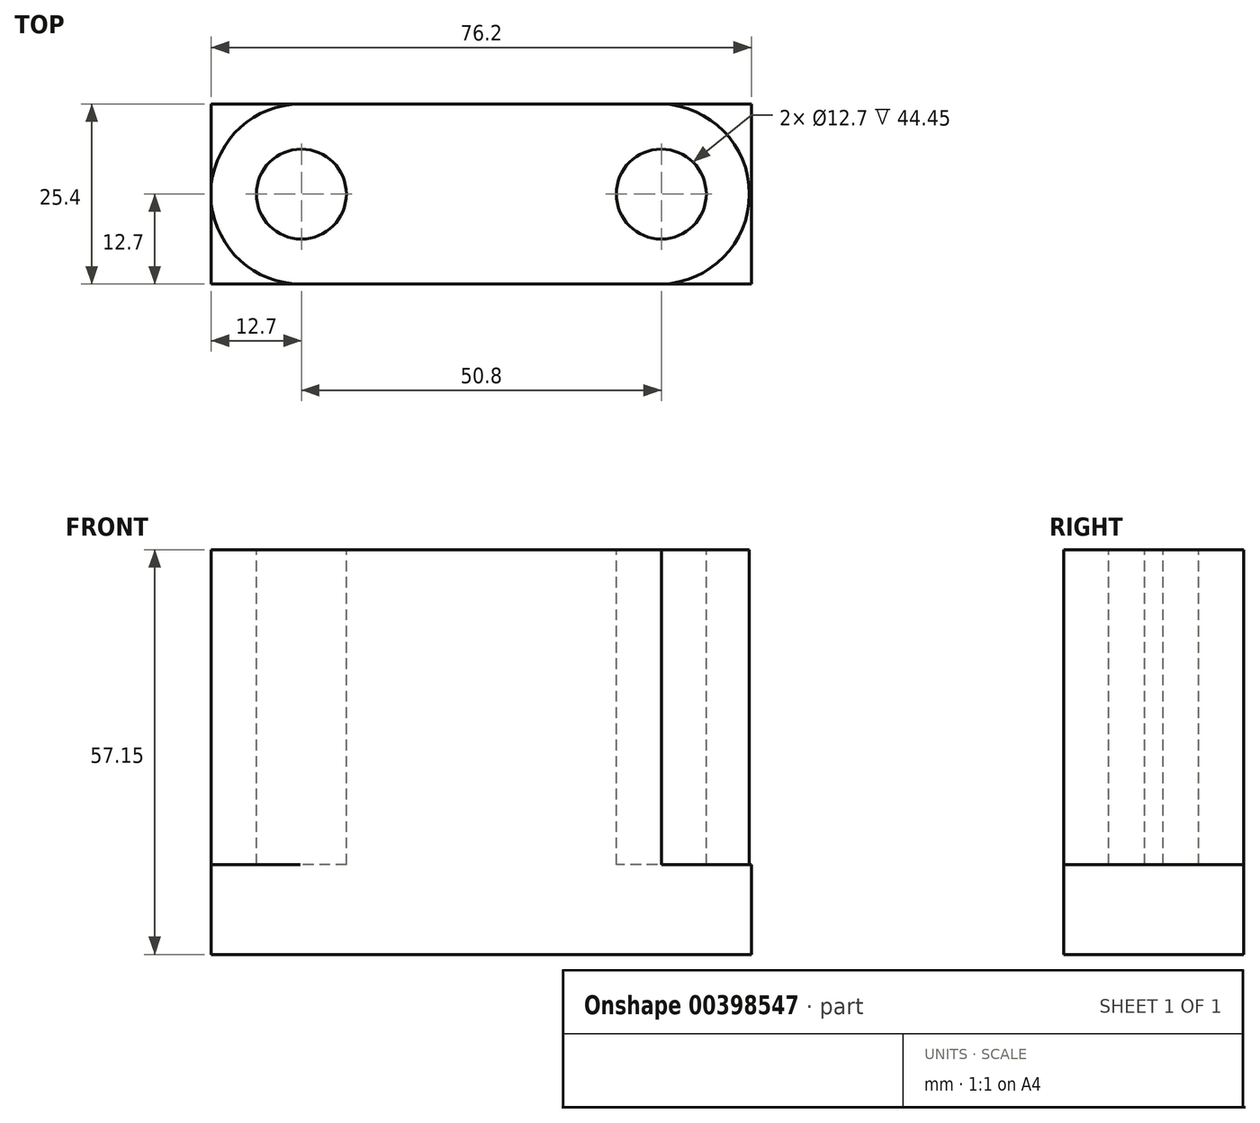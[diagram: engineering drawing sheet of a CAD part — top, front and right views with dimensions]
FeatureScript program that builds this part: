
annotation { "Feature Type Name" : "Feature", "Feature Type Description" : "" }
export const myFeature = defineFeature(function(context is Context, id is Id, definition is map)
    precondition{}
    {
        {
            var Q0;
            Q0=qCreatedBy(makeId("Front.planeOp"),FACE);
            var sketch = newSketch(context, id + "F0", { "sketchPlane" : qUnion([Q0])});
            skLineSegment(sketch, "E0.bottom", {"start": v(0, 0) * mm, "end": v(76.2, 0) * mm});
            skLineSegment(sketch, "E0.top", {"start": v(0, 57.15) * mm, "end": v(76.2, 57.15) * mm});
            skLineSegment(sketch, "E0.left", {"start": v(0, 0) * mm, "end": v(0, 57.15) * mm});
            skLineSegment(sketch, "E0.right", {"start": v(76.2, 0) * mm, "end": v(76.2, 57.15) * mm});
            skSolve(sketch);
        }
        {
            var Q0;
            Q0=makeQuery(id+"F0.imprint","IMPRINT",FACE,{"disambiguationData":[TD([[makeQuery(id+"F0.imprint","IMPRINT",EDGE,{"derivedFrom":sQuery(id+"F0.wireOp",EDGE,"E0.bottom")}),1.0]])]});
            extrude(context, id + "F1", {"entities" : qUnion([Q0]), "depth" : 25.4 * mm});
        }
        {
            var Q0;
            Q0=makeQuery(id+"F1.opExtrude","SWEPT_FACE",FACE,{"disambiguationData":[OSD([sQuery(id+"F0.wireOp",EDGE,"E0.top")])]});
            var sketch = newSketch(context, id + "F2", { "sketchPlane" : qUnion([Q0])});
            skLineSegment(sketch, "E1", {"start": v(25.4, 0) * mm, "end": v(25.4, -25.4) * mm});
            skLineSegment(sketch, "E2", {"start": v(50.8, 0) * mm, "end": v(50.8, -25.4) * mm});
            skCircle(sketch, "E3", {"center": v(63.5, -12.7) * mm, "radius": 6.35 * mm});
            skPoint(sketch, "E3.centerSnap0", {"position": v(50.8, -12.7) * mm});
            skCircle(sketch, "E4", {"center": v(12.7, -12.7) * mm, "radius": 6.35 * mm});
            skArc(sketch, "E5", {"start": v(12.7, 0) * mm, "mid": v(-0.07, -12.7) * mm, "end": v(12.7, -25.4) * mm});
            skArc(sketch, "E6", {"start": v(63.5, -25.4) * mm, "mid": v(75.93, -12.7) * mm, "end": v(63.5, 0) * mm});
            skSolve(sketch);
        }
        {
            var Q0;
            Q0=makeQuery(id+"F2.imprint","IMPRINT",FACE,{"disambiguationData":[TD([[makeQuery(id+"F2.imprint","IMPRINT",EDGE,{"derivedFrom":sQuery(id+"F2.wireOp",EDGE,"E3")}),1.0]])]});
            var Q1;
            Q1=makeQuery(id+"F2.imprint","IMPRINT",FACE,{"disambiguationData":[TD([[makeQuery(id+"F2.imprint","IMPRINT",EDGE,{"derivedFrom":sQuery(id+"F2.wireOp",EDGE,"E4")}),1.0]])]});
            var Q2;
            {var subQ0=sQuery(id+"F2.wireOp",EDGE,"E5");var subQ1=sQuery(id+"F0.wireOp",EDGE,"E0.top");var subQ4=makeQuery(id+"F1.opExtrude","CAP_EDGE",EDGE,{"disambiguationData":[OSD([subQ1])],"isStart":false});var subQ5=makeQuery(id+"F2.imprint","INTERSECT",VERTEX,{"disambiguationData":[OD(1.0)],"derivedFrom":[subQ4,subQ0]});Q2=makeQuery(id+"F2.imprint","IMPRINT",FACE,{"disambiguationData":[TD([[makeQuery(id+"F2.imprint","IMPRINT",EDGE,{"disambiguationData":[TD([[subQ5,1.0]])],"derivedFrom":subQ0}),-1.0]])]});}
            var Q3;
            {var subQ0=sQuery(id+"F2.wireOp",EDGE,"E5");var subQ1=sQuery(id+"F0.wireOp",EDGE,"E0.top");var subQ2=makeQuery(id+"F1.opExtrude","CAP_EDGE",EDGE,{"disambiguationData":[OSD([subQ1])],"isStart":true});var subQ3=makeQuery(id+"F2.imprint","INTERSECT",VERTEX,{"disambiguationData":[OD(1.0)],"derivedFrom":[subQ2,subQ0]});Q3=makeQuery(id+"F2.imprint","IMPRINT",FACE,{"disambiguationData":[TD([[makeQuery(id+"F2.imprint","IMPRINT",EDGE,{"disambiguationData":[TD([[subQ3,-1.0]])],"derivedFrom":subQ0}),-1.0]])]});}
            var Q4;
            {var subQ0=sQuery(id+"F2.wireOp",EDGE,"E6");Q4=makeQuery(id+"F2.imprint","IMPRINT",FACE,{"disambiguationData":[TD([[makeQuery(id+"F2.imprint","IMPRINT",EDGE,{"derivedFrom":subQ0}),-1.0]])]});}
            extrude(context, id + "F3", {"entities" : qUnion([Q0, Q1, Q2, Q3, Q4]), "operationType" : NewBodyOperationType.REMOVE, "oppositeDirection" : true, "depth" : 44.45 * mm});
        }
    });
